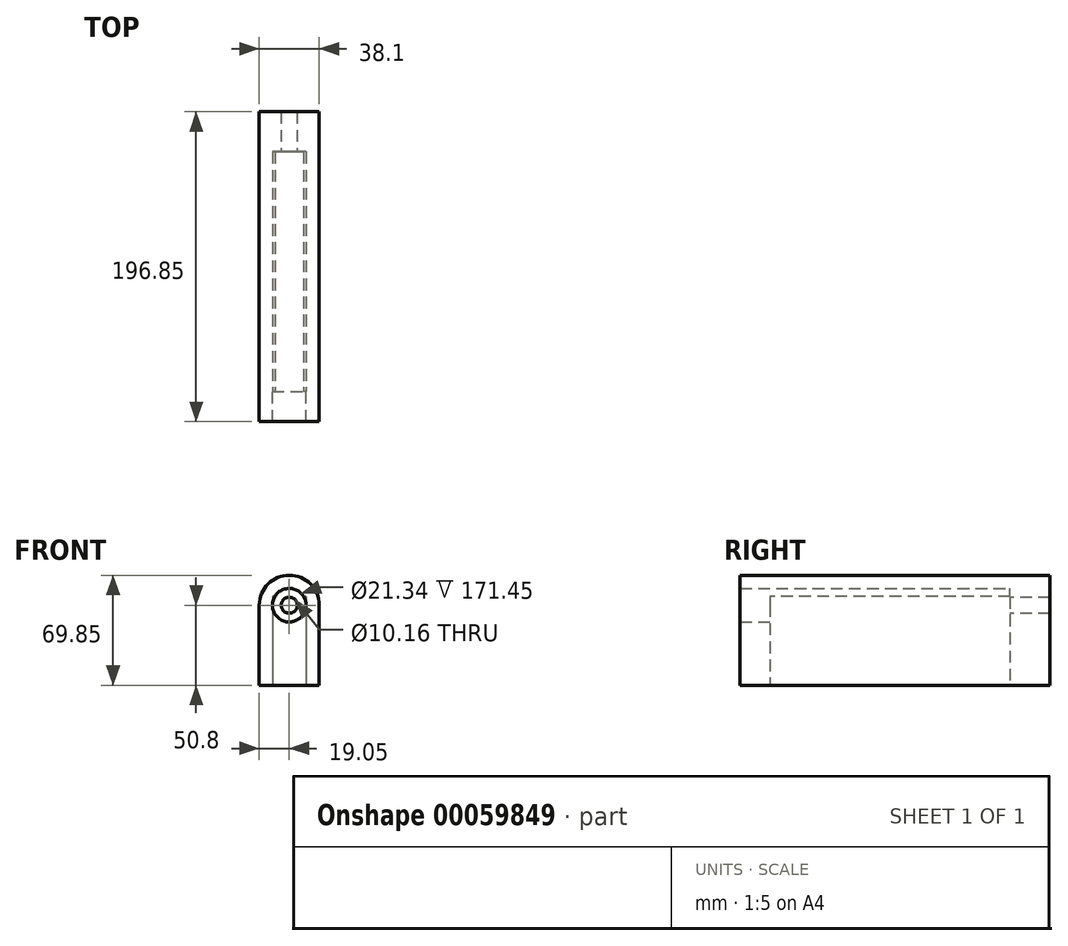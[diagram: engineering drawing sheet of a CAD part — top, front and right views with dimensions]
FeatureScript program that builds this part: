
annotation { "Feature Type Name" : "Feature", "Feature Type Description" : "" }
export const myFeature = defineFeature(function(context is Context, id is Id, definition is map)
    precondition{}
    {
        {
            var Q0;
            Q0=qCreatedBy(makeId("Front.planeOp"),FACE);
            var sketch = newSketch(context, id + "F0", { "sketchPlane" : qUnion([Q0])});
            skArc(sketch, "E0", {"start": v(19.05, 0) * mm, "mid": v(0, 19.05) * mm, "end": v(-19.05, 0) * mm});
            skLineSegment(sketch, "E1.top", {"start": v(-19.05, -50.8) * mm, "end": v(19.05, -50.8) * mm});
            skLineSegment(sketch, "E1.left", {"start": v(-19.05, 0) * mm, "end": v(-19.05, -50.8) * mm});
            skLineSegment(sketch, "E1.right", {"start": v(19.05, 0) * mm, "end": v(19.05, -50.8) * mm});
            skCircle(sketch, "E2", {"center": v(0, 0) * mm, "radius": 10.67 * mm});
            skLineSegment(sketch, "E3", {"start": v(18.21, 5.59) * mm, "end": v(9.09, 5.59) * mm});
            skLineSegment(sketch, "E4", {"start": v(9.09, 5.59) * mm, "end": v(-9.09, 5.59) * mm, "construction": true});
            skLineSegment(sketch, "E5", {"start": v(-9.09, 5.59) * mm, "end": v(-18.21, 5.59) * mm});
            skLineSegment(sketch, "E6", {"start": v(-10.67, 5.59) * mm, "end": v(-10.67, -50.8) * mm});
            skLineSegment(sketch, "E7", {"start": v(10.67, 5.59) * mm, "end": v(10.67, -50.8) * mm});
            skSolve(sketch);
        }
        {
            var Q0;
            Q0=makeQuery(id+"F0.imprint","IMPRINT",FACE,{"disambiguationData":[TD([[makeQuery(id+"F0.imprint","IMPRINT",EDGE,{"derivedFrom":sQuery(id+"F0.wireOp",EDGE,"E0")}),1.0]])]});
            var Q1;
            {var subQ0=sQuery(id+"F0.wireOp",EDGE,"E3");Q1=makeQuery(id+"F0.imprint","IMPRINT",FACE,{"disambiguationData":[TD([[makeQuery(id+"F0.imprint","IMPRINT",EDGE,{"derivedFrom":subQ0}),-1.0]])]});}
            var Q2;
            {var subQ0=sQuery(id+"F0.wireOp",EDGE,"E6");var subQ1=sQuery(id+"F0.wireOp",EDGE,"E1.top");var subQ2=makeQuery(id+"F0.imprint","INTERSECT",VERTEX,{"derivedFrom":[subQ1,subQ0]});Q2=makeQuery(id+"F0.imprint","IMPRINT",FACE,{"disambiguationData":[TD([[makeQuery(id+"F0.imprint","IMPRINT",EDGE,{"disambiguationData":[TD([[subQ2,-1.0]])],"derivedFrom":subQ1}),1.0]])]});}
            var Q3;
            {var subQ0=sQuery(id+"F0.wireOp",EDGE,"E3");var subQ1=sQuery(id+"F0.wireOp",EDGE,"E2");var subQ2=makeQuery(id+"F0.imprint","INTERSECT",VERTEX,{"derivedFrom":[subQ1,subQ0]});Q3=makeQuery(id+"F0.imprint","IMPRINT",FACE,{"disambiguationData":[TD([[makeQuery(id+"F0.imprint","IMPRINT",EDGE,{"disambiguationData":[TD([[subQ2,1.0]])],"derivedFrom":subQ1}),-1.0]])]});}
            var Q4;
            {var subQ0=sQuery(id+"F0.wireOp",EDGE,"E5");var subQ1=sQuery(id+"F0.wireOp",EDGE,"E2");var subQ2=makeQuery(id+"F0.imprint","INTERSECT",VERTEX,{"derivedFrom":[subQ1,subQ0]});Q4=makeQuery(id+"F0.imprint","IMPRINT",FACE,{"disambiguationData":[TD([[makeQuery(id+"F0.imprint","IMPRINT",EDGE,{"disambiguationData":[TD([[subQ2,-1.0]])],"derivedFrom":subQ1}),-1.0]])]});}
            extrude(context, id + "F1", {"entities" : qUnion([Q0, Q1, Q2, Q3, Q4]), "depth" : 19.05 * mm});
        }
        {
            var Q0;
            {var subQ5=sQuery(id+"F0.wireOp",EDGE,"E1.right");Q0=makeQuery(id+"F0.imprint","IMPRINT",FACE,{"disambiguationData":[TD([[makeQuery(id+"F0.imprint","IMPRINT",EDGE,{"derivedFrom":subQ5}),-1.0]])]});}
            var Q1;
            {var subQ0=sQuery(id+"F0.wireOp",EDGE,"E3");var subQ4=sQuery(id+"F0.wireOp",EDGE,"E0");var subQ5=makeQuery(id+"F0.imprint","INTERSECT",VERTEX,{"derivedFrom":[subQ4,subQ0]});Q1=makeQuery(id+"F0.imprint","IMPRINT",FACE,{"disambiguationData":[TD([[makeQuery(id+"F0.imprint","IMPRINT",EDGE,{"disambiguationData":[TD([[subQ5,-1.0]])],"derivedFrom":subQ4}),1.0]])]});}
            var Q2;
            {var subQ5=sQuery(id+"F0.wireOp",EDGE,"E1.left");Q2=makeQuery(id+"F0.imprint","IMPRINT",FACE,{"disambiguationData":[TD([[makeQuery(id+"F0.imprint","IMPRINT",EDGE,{"derivedFrom":subQ5}),1.0]])]});}
            extrude(context, id + "F2", {"entities" : qUnion([Q0, Q1, Q2]), "operationType" : NewBodyOperationType.ADD, "oppositeDirection" : true, "depth" : 152.4 * mm});
        }
        {
            var Q0;
            Q0=makeQuery(id+"F2.opExtrude","CAP_FACE",FACE,{"disambiguationData":[OSD([sQuery(id+"F0.wireOp",EDGE,"E0"),sQuery(id+"F0.wireOp",EDGE,"E1.top"),sQuery(id+"F0.wireOp",EDGE,"E1.left"),sQuery(id+"F0.wireOp",EDGE,"E1.right"),sQuery(id+"F0.wireOp",EDGE,"E2"),sQuery(id+"F0.wireOp",EDGE,"E3"),sQuery(id+"F0.wireOp",EDGE,"E5"),sQuery(id+"F0.wireOp",EDGE,"E6"),sQuery(id+"F0.wireOp",EDGE,"E7")])],"isStart":false});
            var sketch = newSketch(context, id + "F3", { "sketchPlane" : qUnion([Q0])});
            skArc(sketch, "E8.0", {"start": v(-19.05, 0) * mm, "mid": v(0, 19.05) * mm, "end": v(19.05, 0) * mm});
            skLineSegment(sketch, "E9.0", {"start": v(-19.05, 0) * mm, "end": v(-19.05, -50.8) * mm});
            skLineSegment(sketch, "E10.0", {"start": v(19.05, 0) * mm, "end": v(19.05, -50.8) * mm});
            skLineSegment(sketch, "E11.0", {"start": v(19.05, -50.8) * mm, "end": v(-19.05, -50.8) * mm});
            skCircle(sketch, "E12", {"center": v(0, 0) * mm, "radius": 5.08 * mm});
            skCircle(sketch, "E13.0", {"center": v(0, 0) * mm, "radius": 10.67 * mm});
            skSolve(sketch);
        }
        {
            var Q0;
            Q0 = qSketchRegion(id + "F3", true);
            var Q1;
            Q1=makeQuery(id+"F3.imprint","IMPRINT",FACE,{"disambiguationData":[TD([[makeQuery(id+"F3.imprint","IMPRINT",EDGE,{"derivedFrom":sQuery(id+"F3.wireOp",EDGE,"E12")}),-1.0]])]});
            extrude(context, id + "F4", {"entities" : qUnion([Q0, Q1]), "operationType" : NewBodyOperationType.ADD, "depth" : 25.4 * mm});
        }
    });
